# Revit family: IS_TonicII_E3974_BIM_DE
name_source: partatom
category: Plumbing Fixtures
revit_build: Autodesk Revit MEP 2016 (Build: 20161004_0715(x64)
units: mm (PartAtom-declared; Revit-internal decimal feet)

## family parameters
Always vertical = No
Cut with Voids When Loaded = No
OmniClass Number = 23.45.05.14.21
OmniClass Title = Bathtubs
Part Type = Normal
Room Calculation Point = No
Round Connector Dimension = Use Diameter
Shared = No
Work Plane-Based = No

## types (1)
- E397401 TONIC II rectangular bath tub 1800x800mm
    Accessories = www.idealstandard.de\ersatzteile
    AssetType = Fixed
    BIMObjectName = ISI_IdealStandard_Baths_TONICII_E397401
    BIMobject category = Bath & Spas
    BOSUseNativeGeometries = 1
    BarCode = 5017830487975
    Brand = Ideal Standard
    Brand url = http://www.idealstandard.de
    CodePerformance = DIN EN 14516, DIN EN 232, DIN EN
    Color = White
    ConnectionType = Plumbing
    Cost = 0 $
    CurrencyUnit = €
    CurrentRevision = 1
    Description = E397401 TONIC II rectangular bath tub 1800x800mm
    DrainSize = 0 mm  [stored 0 ft]
    DurationUnit = Jaar
    EAN code = https://5017830487975
    Edition number = 1
    ExpectedLife = 25
    Features = TONIC II rectangular bath tub 1800x800mm
    Finish = White
    HasGrabHandles = No
    IFC Classification = Sanitary Terminal
    IfcExportAs = Sanitary terminal type
    IfcExportType = BATH
    Installation instructions = http://www.idealstandard.de
    InstallationInstructions = www.idealstandard.de\produkte
    LinearUnits = millimetres
    MainColor = White
    MaintenanceInformation = www.idealstandard.de
    Manufacturer = http://www.idealstandard.de
    Manufacturer name = Ideal Standard
    ManufacturerURL = http://www.idealstandard.de
    Material = Sanitary Brass
    Material main = Acrylic
    MaterialThickness = 0 mm  [stored 0 ft]
    Model = E397401
    ModelNumber = E397401
    ModelReference = E397401 TONIC II rectangular bath tub 1800x800mm
    NBS Reference Code = 35-06-08
    NBS Reference Description = Baths
    Name = ISI_IdealStandard_Baths_TONICII_E397401
    NettWeight = 30,4 kg
    Nominal height = 490
    Nominal width = 800
    NominalHeight = 630 mm
    NominalLength = 1795 mm
    NominalWidth = 795 mm  [stored 2.60827 ft]
    OmniClass Code = 23-31 15 00
    OmniClass Description = Bathtubs
    Product Guid = 406d65de-e902-408e-9c95-8b8c11d8a369
    Product SKU = E3974
    Product certification = DIN EN 14516, DIN EN 232, DIN EN
    Product data url = https://bimobject.com
    Product family = TONIC II
    Product group = Bath Tub
    Product name = TONIC II rectangular bath tub 1800x800mm
    Product url = http://www.idealstandard.de
    ProductInformation = www.idealstandard.de/produkte
    QR code = http://bimobject.com
    Shape = Rectangular
    Size = 1795x795x630 mm
    Space = Internal
    SpareParts = www.idealstandard.de/ersatzteile
    Technical description = http://www.idealstandard.de
    URL = http://www.idealstandard.de
    Uniclass 2.0 Code = PR-35-06-08
    Uniclass 2.0 Description = Baths
    Uniclass 2015 Code = Pr_40_20_06_08
    Uniclass 2015 Name = Baths
    Uniclass2015Code = Pr_40_20_06_08
    Uniclass2015Title = Baths
    Uniclass2015Version = Products v1.1
    VolumeUnits = Litres
    Weight Net (Kg) = 30.4

note: [stored X ft] marks values corroborated as IEEE doubles in the binary element streams (Revit-internal decimal feet)

## geometry (parser evidence)
native form markers: Blend x2, Sweep x3
no freeform markers — native parametric forms only
